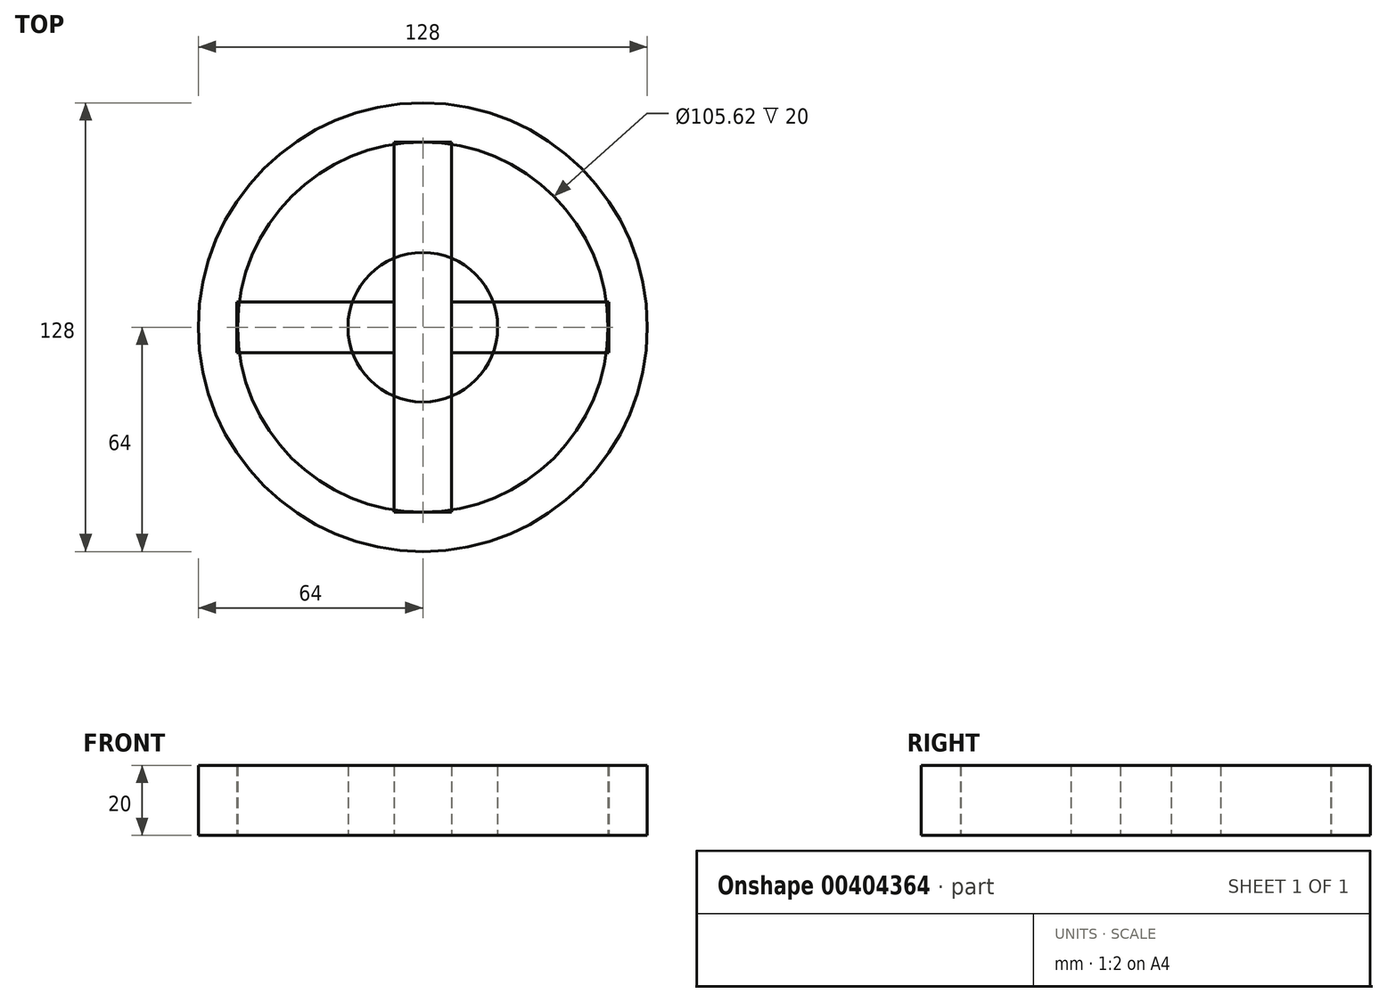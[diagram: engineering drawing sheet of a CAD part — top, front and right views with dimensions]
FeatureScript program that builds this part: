
annotation { "Feature Type Name" : "Feature", "Feature Type Description" : "" }
export const myFeature = defineFeature(function(context is Context, id is Id, definition is map)
    precondition{}
    {
        {
            var Q0;
            Q0=qCreatedBy(makeId("Top.planeOp"),FACE);
            var sketch = newSketch(context, id + "F0", { "sketchPlane" : qUnion([Q0])});
            skCircle(sketch, "E0", {"center": v(0, 0) * mm, "radius": 64 * mm});
            skCircle(sketch, "E1", {"center": v(0, 0) * mm, "radius": 52.81 * mm});
            skCircle(sketch, "E2", {"center": v(0, 0) * mm, "radius": 18.76 * mm});
            skCircle(sketch, "E3", {"center": v(0, 0) * mm, "radius": 8.97 * mm});
            skSolve(sketch);
        }
        {
            var Q0;
            Q0 = qSketchRegion(id + "F0", true);
            extrude(context, id + "F1", {"entities" : qUnion([Q0]), "depth" : 20 * mm});
        }
        {
            var Q0;
            Q0=qCreatedBy(makeId("Top.planeOp"),FACE);
            var sketch = newSketch(context, id + "F2", { "sketchPlane" : qUnion([Q0])});
            skCircle(sketch, "E4", {"center": v(0, 0) * mm, "radius": 21.32 * mm});
            skSolve(sketch);
        }
        {
            var Q0;
            Q0=makeQuery(id+"F2.imprint","IMPRINT",FACE,{"disambiguationData":[TD([[makeQuery(id+"F2.imprint","IMPRINT",EDGE,{"derivedFrom":sQuery(id+"F2.wireOp",EDGE,"E4")}),1.0]])]});
            extrude(context, id + "F3", {"entities" : qUnion([Q0]), "depth" : 20 * mm});
        }
        {
            var Q0;
            Q0=qCreatedBy(makeId("Top.planeOp"),FACE);
            var sketch = newSketch(context, id + "F4", { "sketchPlane" : qUnion([Q0])});
            skLineSegment(sketch, "E5.bottom", {"start": v(8.18, 52.73) * mm, "end": v(-8.18, 52.73) * mm});
            skLineSegment(sketch, "E5.top", {"start": v(8.18, -52.73) * mm, "end": v(-8.18, -52.73) * mm});
            skLineSegment(sketch, "E5.left", {"start": v(8.18, 52.73) * mm, "end": v(8.18, -52.73) * mm});
            skLineSegment(sketch, "E5.right", {"start": v(-8.18, 52.73) * mm, "end": v(-8.18, -52.73) * mm});
            skPoint(sketch, "E5.middle", {"position": v(0, 0) * mm});
            skSolve(sketch);
        }
        {
            var Q0;
            Q0 = qSketchRegion(id + "F4", true);
            var sketch = newSketch(context, id + "F5", { "sketchPlane" : qUnion([Q0])});
            skLineSegment(sketch, "E6.bottom", {"start": v(-53, -7.23) * mm, "end": v(53, -7.23) * mm});
            skLineSegment(sketch, "E6.top", {"start": v(-53, 7.23) * mm, "end": v(53, 7.23) * mm});
            skLineSegment(sketch, "E6.left", {"start": v(-53, -7.23) * mm, "end": v(-53, 7.23) * mm});
            skLineSegment(sketch, "E6.right", {"start": v(53, -7.23) * mm, "end": v(53, 7.23) * mm});
            skPoint(sketch, "E6.middle", {"position": v(0, 0) * mm});
            skSolve(sketch);
        }
        {
            var Q0;
            {var subQ0=sQuery(id+"F5.wireOp",EDGE,"E6.left");Q0=makeQuery(id+"F5.imprint","IMPRINT",FACE,{"disambiguationData":[TD([[makeQuery(id+"F5.imprint","IMPRINT",EDGE,{"derivedFrom":subQ0}),-1.0]])]});}
            var Q1;
            {var subQ0=sQuery(id+"F5.wireOp",EDGE,"E6.right");Q1=makeQuery(id+"F5.imprint","IMPRINT",FACE,{"disambiguationData":[TD([[makeQuery(id+"F5.imprint","IMPRINT",EDGE,{"derivedFrom":subQ0}),1.0]])]});}
            var Q2;
            Q2=makeQuery(id+"F4.imprint","IMPRINT",FACE,{"disambiguationData":[TD([[makeQuery(id+"F4.imprint","IMPRINT",EDGE,{"derivedFrom":sQuery(id+"F4.wireOp",EDGE,"E5.bottom")}),1.0]])]});
            extrude(context, id + "F6", {"entities" : qUnion([Q0, Q1, Q2]), "depth" : 20 * mm});
        }
    });
